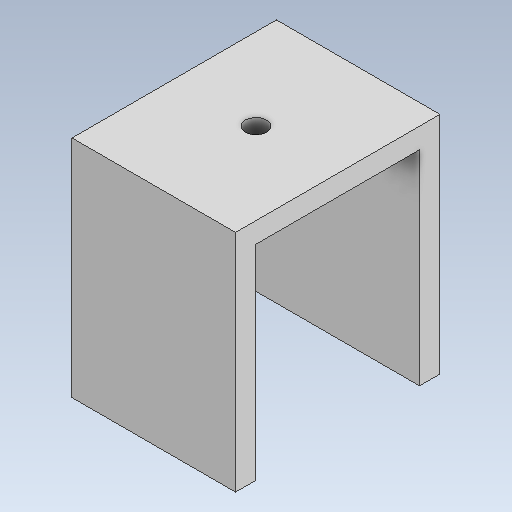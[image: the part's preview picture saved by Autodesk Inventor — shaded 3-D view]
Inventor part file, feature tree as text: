
AUTODESK INVENTOR PART (.ipt)
format: ipt  version: 2020.3 (Build 243373000, 373)  size: 152,576 bytes
history: native  units: mm
features: sketch x7, extrude x7, projected_geometry x3, plane x1
ambient origin geometry x8: Origin, YZ Plane, XZ Plane, XY Plane, X Axis, Y Axis, Z Axis, Center Point
bodies: Solid1 (feature_tree)
feature tree (18):
  sketch  "Sketch1"  dims[d0=20.0mm d1=50.0mm]
  plane  "Work Plane1"
  extrude  "Extrusion2"  Depth=50.0mm
  extrude  "Extrusion3"  Depth=5.0mm TaperAngle=0.0deg
  extrude  "Extrusion4"  Depth=5.0mm TaperAngle=0.0deg
  extrude  "Extrusion5"  Depth=5.0mm
  extrude  "Extrusion6"  Depth=10.0mm
  extrude  "Extrusion7"  Depth=10.0mm
  extrude  "Extrusion8"  Depth=5.0mm
  sketch  "Sketch2"  dims[d4=40.0mm d5=5.0mm d6=0.0mm]
  sketch  "Sketch3"  dims[d7=5.0mm d8=0.0mm d9=5.0mm d10=0.0mm]
  projected_geometry  "Projected Loop1"
  projected_geometry  "Projected Loop2"
  sketch  "Sketch4"  dims[d11=5.0mm d12=0.0mm d13=5.2mm]
  projected_geometry  "Projected Loop3"
  sketch  "Sketch5"  dims[d14=10.0mm d15=0.0mm d16=10.0mm]
  sketch  "Sketch6"  dims[d17=50.0mm d18=10.0mm]
  sketch  "Sketch7"  dims[d19=5.0mm d20=0.0mm d21=5.0mm d22=50.0mm d23=0.0mm]
